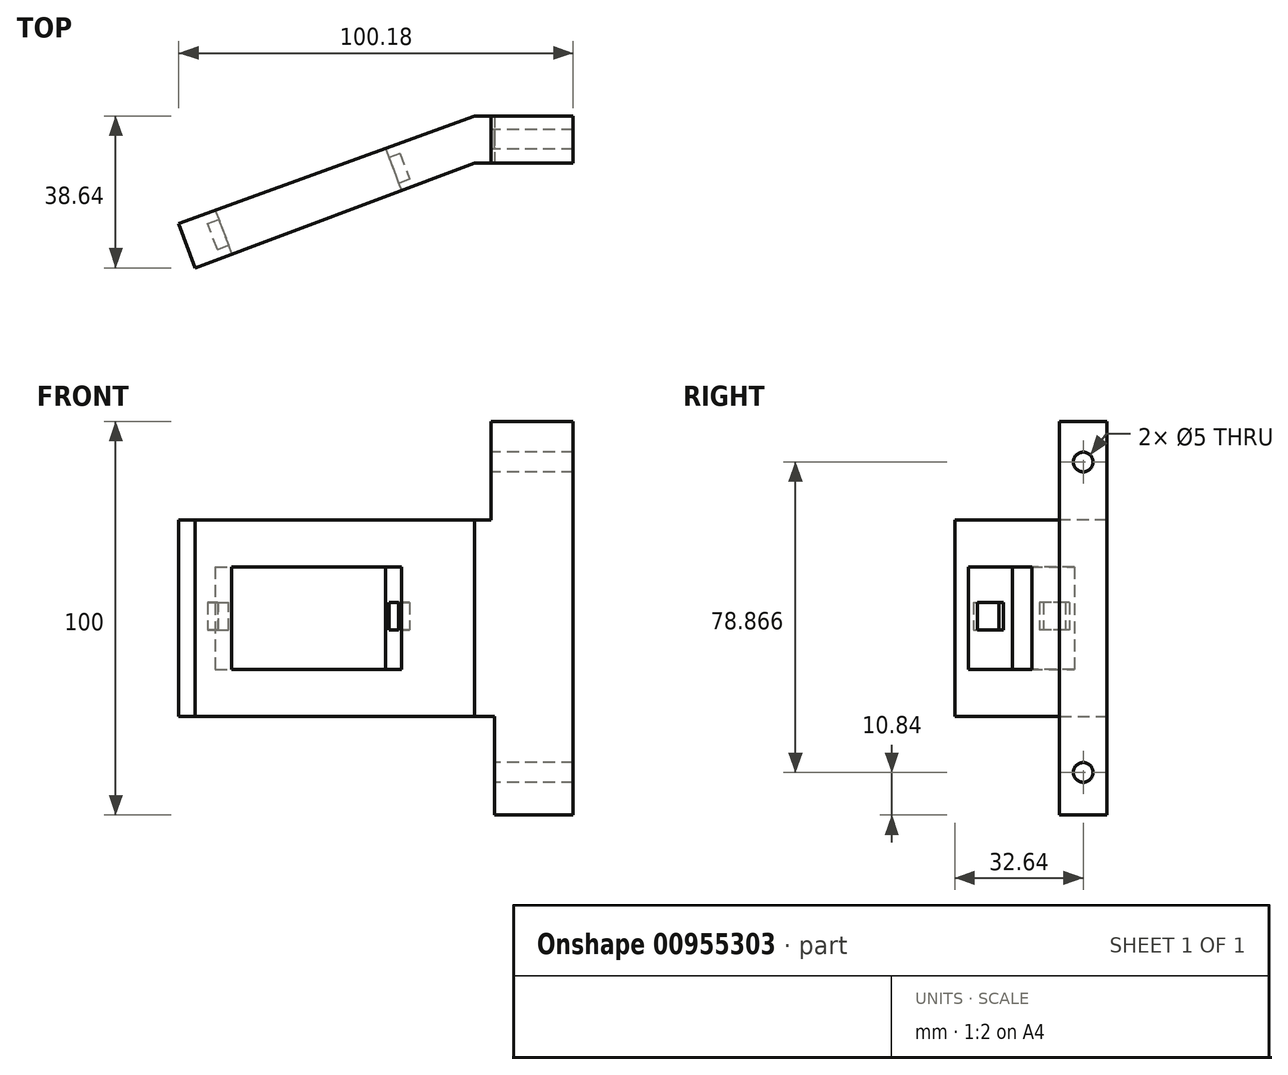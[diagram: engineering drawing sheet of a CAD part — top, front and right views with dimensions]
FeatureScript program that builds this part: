
annotation { "Feature Type Name" : "Feature", "Feature Type Description" : "" }
export const myFeature = defineFeature(function(context is Context, id is Id, definition is map)
    precondition{}
    {
        {
            var Q0;
            Q0=qCreatedBy(makeId("Top.planeOp"),FACE);
            var sketch = newSketch(context, id + "F0", { "sketchPlane" : qUnion([Q0])});
            skLineSegment(sketch, "E0", {"start": v(0, 0) * mm, "end": v(0, 12) * mm});
            skLineSegment(sketch, "E1", {"start": v(0, 12) * mm, "end": v(-25, 12) * mm});
            skLineSegment(sketch, "E2", {"start": v(-25, 12) * mm, "end": v(-100.18, -15.36) * mm});
            skLineSegment(sketch, "E3", {"start": v(-100.18, -15.36) * mm, "end": v(-96.07, -26.64) * mm});
            skLineSegment(sketch, "E4", {"start": v(0, 0) * mm, "end": v(-25, 0) * mm});
            skLineSegment(sketch, "E5", {"start": v(-96.07, -26.64) * mm, "end": v(-25, 0) * mm});
            skSolve(sketch);
        }
        {
            var Q0;
            Q0 = qSketchRegion(id + "F0", true);
            extrude(context, id + "F1", {"entities" : qUnion([Q0]), "depth" : 100 * mm, "offsetDistance" : 25 * mm});
        }
        {
            var Q0;
            Q0=makeQuery(id+"F1.opExtrude","SWEPT_FACE",FACE,{"disambiguationData":[OSD([sQuery(id+"F0.wireOp",EDGE,"E5")])]});
            cPlane(context, id + "F2", {"entities" : qUnion([Q0]), "cplaneType" : CPlaneType.OFFSET, "offset" : 0 * mm, "width" : 150 * mm, "height" : 150 * mm});
        }
        {
            var Q0;
            Q0=qCreatedBy(id+"F2.planeOp",FACE);
            var sketch = newSketch(context, id + "F3", { "sketchPlane" : qUnion([Q0])});
            skLineSegment(sketch, "E6.bottom", {"start": v(-89.3, 63) * mm, "end": v(-43.3, 63) * mm});
            skLineSegment(sketch, "E6.top", {"start": v(-89.3, 37) * mm, "end": v(-43.3, 37) * mm});
            skLineSegment(sketch, "E6.left", {"start": v(-89.3, 63) * mm, "end": v(-89.3, 37) * mm});
            skLineSegment(sketch, "E6.right", {"start": v(-43.3, 63) * mm, "end": v(-43.3, 37) * mm});
            skSolve(sketch);
        }
        {
            var Q0;
            Q0 = qSketchRegion(id + "F3", true);
            extrude(context, id + "F4", {"entities" : qUnion([Q0]), "operationType" : NewBodyOperationType.REMOVE, "oppositeDirection" : true, "depth" : 25 * mm, "offsetDistance" : 25 * mm});
        }
        {
            var Q0;
            Q0=makeQuery(id+"F1.opExtrude","CAP_FACE",FACE,{"disambiguationData":[OSD([sQuery(id+"F0.wireOp",EDGE,"E0"),sQuery(id+"F0.wireOp",EDGE,"E1"),sQuery(id+"F0.wireOp",EDGE,"E2"),sQuery(id+"F0.wireOp",EDGE,"E3"),sQuery(id+"F0.wireOp",EDGE,"E4"),sQuery(id+"F0.wireOp",EDGE,"E5")])],"isStart":false});
            var sketch = newSketch(context, id + "F5", { "sketchPlane" : qUnion([Q0])});
            skLineSegment(sketch, "E7.bottom", {"start": v(-116.92, 30.4) * mm, "end": v(-20, 30.4) * mm});
            skLineSegment(sketch, "E7.top", {"start": v(-116.92, -38.36) * mm, "end": v(-20, -38.36) * mm});
            skLineSegment(sketch, "E7.left", {"start": v(-116.92, 30.4) * mm, "end": v(-116.92, -38.36) * mm});
            skLineSegment(sketch, "E7.right", {"start": v(-20, 30.4) * mm, "end": v(-20, -38.36) * mm});
            skSolve(sketch);
        }
        {
            var Q0;
            {var subQ5=makeQuery(id+"F1.opExtrude","CAP_EDGE",EDGE,{"disambiguationData":[OSD([sQuery(id+"F0.wireOp",EDGE,"E0")])],"isStart":false});Q0=makeQuery(id+"F5.imprint","IMPRINT",FACE,{"disambiguationData":[TD([[makeQuery(id+"F5.imprint","IMPRINT",EDGE,{"derivedFrom":subQ5}),1.0]])]});}
            cPlane(context, id + "F6", {"entities" : qUnion([Q0]), "cplaneType" : CPlaneType.OFFSET, "offset" : 5 * mm, "width" : 150 * mm, "height" : 150 * mm});
        }
        {
            var Q0;
            Q0=qCreatedBy(id+"F6.planeOp",FACE);
            var sketch = newSketch(context, id + "F7", { "sketchPlane" : qUnion([Q0])});
            skLineSegment(sketch, "E8.bottom", {"start": v(-119.42, 33.1) * mm, "end": v(-20.8, 33.1) * mm});
            skLineSegment(sketch, "E8.top", {"start": v(-119.42, -42.01) * mm, "end": v(-20.8, -42.01) * mm});
            skLineSegment(sketch, "E8.left", {"start": v(-119.42, 33.1) * mm, "end": v(-119.42, -42.01) * mm});
            skLineSegment(sketch, "E8.right", {"start": v(-20.8, 33.1) * mm, "end": v(-20.8, -42.01) * mm});
            skSolve(sketch);
        }
        {
            var Q0;
            Q0 = qSketchRegion(id + "F7", true);
            extrude(context, id + "F8", {"entities" : qUnion([Q0]), "operationType" : NewBodyOperationType.REMOVE, "oppositeDirection" : true, "depth" : 30 * mm, "offsetDistance" : 25 * mm});
        }
        {
            var Q0;
            Q0=makeQuery(id+"F1.opExtrude","CAP_FACE",FACE,{"disambiguationData":[OSD([sQuery(id+"F0.wireOp",EDGE,"E0"),sQuery(id+"F0.wireOp",EDGE,"E1"),sQuery(id+"F0.wireOp",EDGE,"E2"),sQuery(id+"F0.wireOp",EDGE,"E3"),sQuery(id+"F0.wireOp",EDGE,"E4"),sQuery(id+"F0.wireOp",EDGE,"E5")])],"isStart":true});
            cPlane(context, id + "F9", {"entities" : qUnion([Q0]), "cplaneType" : CPlaneType.OFFSET, "offset" : 5 * mm, "width" : 150 * mm, "height" : 150 * mm});
        }
        {
            var Q0;
            Q0=qCreatedBy(id+"F9.planeOp",FACE);
            var sketch = newSketch(context, id + "F10", { "sketchPlane" : qUnion([Q0])});
            skLineSegment(sketch, "E9.bottom", {"start": v(-117.91, 40.15) * mm, "end": v(-20, 40.15) * mm});
            skLineSegment(sketch, "E9.top", {"start": v(-117.91, -43.8) * mm, "end": v(-20, -43.8) * mm});
            skLineSegment(sketch, "E9.left", {"start": v(-117.91, 40.15) * mm, "end": v(-117.91, -43.8) * mm});
            skLineSegment(sketch, "E9.right", {"start": v(-20, 40.15) * mm, "end": v(-20, -43.8) * mm});
            skSolve(sketch);
        }
        {
            var Q0;
            Q0 = qSketchRegion(id + "F10", true);
            extrude(context, id + "F11", {"entities" : qUnion([Q0]), "operationType" : NewBodyOperationType.REMOVE, "oppositeDirection" : true, "depth" : 30 * mm, "offsetDistance" : 25 * mm});
        }
        {
            var Q0;
            Q0=makeQuery(id+"F8.boolean.opBoolean","COPY",FACE,{"derivedFrom":makeQuery(id+"F8.opExtrude","SWEPT_FACE",FACE,{"disambiguationData":[OSD([sQuery(id+"F7.wireOp",EDGE,"E8.right")])]})});
            cPlane(context, id + "F12", {"entities" : qUnion([Q0]), "cplaneType" : CPlaneType.OFFSET, "offset" : 5 * mm, "width" : 150 * mm, "height" : 150 * mm});
        }
        {
            var Q0;
            Q0=qCreatedBy(id+"F12.planeOp",FACE);
            var sketch = newSketch(context, id + "F13", { "sketchPlane" : qUnion([Q0])});
            skCircle(sketch, "E10", {"center": v(-6, 89.7) * mm, "radius": 2.5 * mm});
            skSolve(sketch);
        }
        {
            var Q0;
            Q0=makeQuery(id+"F11.boolean.opBoolean","COPY",FACE,{"derivedFrom":makeQuery(id+"F11.opExtrude","SWEPT_FACE",FACE,{"disambiguationData":[OSD([sQuery(id+"F10.wireOp",EDGE,"E9.right")])]})});
            cPlane(context, id + "F14", {"entities" : qUnion([Q0]), "cplaneType" : CPlaneType.OFFSET, "offset" : 5 * mm, "width" : 150 * mm, "height" : 150 * mm});
        }
        {
            var Q0;
            Q0=qCreatedBy(id+"F14.planeOp",FACE);
            var sketch = newSketch(context, id + "F15", { "sketchPlane" : qUnion([Q0])});
            skCircle(sketch, "E11", {"center": v(-6, 10.84) * mm, "radius": 2.5 * mm});
            skSolve(sketch);
        }
        {
            var Q0;
            Q0 = qSketchRegion(id + "F15", true);
            extrude(context, id + "F16", {"entities" : qUnion([Q0]), "operationType" : NewBodyOperationType.REMOVE, "oppositeDirection" : true, "depth" : 30 * mm, "offsetDistance" : 25 * mm});
        }
        {
            var Q0;
            Q0=makeQuery(id+"F13.imprint","IMPRINT",FACE,{"disambiguationData":[TD([[makeQuery(id+"F13.imprint","IMPRINT",EDGE,{"derivedFrom":sQuery(id+"F13.wireOp",EDGE,"E10")}),1.0]])]});
            var Q1;
            Q1=sQuery(id+"F13.wireOp",EDGE,"E10");
            extrude(context, id + "F17", {"entities" : qUnion([Q0]), "operationType" : NewBodyOperationType.REMOVE, "surfaceEntities" : qUnion([Q1]), "oppositeDirection" : true, "depth" : 30 * mm, "offsetDistance" : 25 * mm});
        }
        {
            var Q0;
            Q0=makeQuery(id+"F4.boolean.opBoolean","COPY",FACE,{"derivedFrom":makeQuery(id+"F4.opExtrude","SWEPT_FACE",FACE,{"disambiguationData":[OSD([sQuery(id+"F3.wireOp",EDGE,"E6.right")])]})});
            cPlane(context, id + "F18", {"entities" : qUnion([Q0]), "cplaneType" : CPlaneType.OFFSET, "offset" : 5 * mm, "width" : 150 * mm, "height" : 150 * mm});
        }
        {
            var Q0;
            Q0=qCreatedBy(id+"F18.planeOp",FACE);
            var sketch = newSketch(context, id + "F19", { "sketchPlane" : qUnion([Q0])});
            skLineSegment(sketch, "E12.bottom", {"start": v(-17.74, 54) * mm, "end": v(-10.74, 54) * mm});
            skLineSegment(sketch, "E12.top", {"start": v(-17.74, 47) * mm, "end": v(-10.74, 47) * mm});
            skLineSegment(sketch, "E12.left", {"start": v(-17.74, 54) * mm, "end": v(-17.74, 47) * mm});
            skLineSegment(sketch, "E12.right", {"start": v(-10.74, 54) * mm, "end": v(-10.74, 47) * mm});
            skSolve(sketch);
        }
        {
            var Q0;
            Q0=makeQuery(id+"F19.imprint","IMPRINT",FACE,{"disambiguationData":[TD([[makeQuery(id+"F19.imprint","IMPRINT",EDGE,{"derivedFrom":sQuery(id+"F19.wireOp",EDGE,"E12.bottom")}),-1.0]])]});
            extrude(context, id + "F20", {"entities" : qUnion([Q0]), "operationType" : NewBodyOperationType.REMOVE, "oppositeDirection" : true, "depth" : 8 * mm, "offsetDistance" : 25 * mm});
        }
        {
            var Q0;
            Q0=makeQuery(id+"F4.boolean.opBoolean","COPY",FACE,{"derivedFrom":makeQuery(id+"F4.opExtrude","SWEPT_FACE",FACE,{"disambiguationData":[OSD([sQuery(id+"F3.wireOp",EDGE,"E6.left")])]})});
            cPlane(context, id + "F21", {"entities" : qUnion([Q0]), "cplaneType" : CPlaneType.OFFSET, "offset" : 5 * mm, "width" : 150 * mm, "height" : 150 * mm});
        }
        {
            var Q0;
            Q0=qCreatedBy(id+"F21.planeOp",FACE);
            var sketch = newSketch(context, id + "F22", { "sketchPlane" : qUnion([Q0])});
            skLineSegment(sketch, "E13.bottom", {"start": v(11.18, 54) * mm, "end": v(18.18, 54) * mm});
            skLineSegment(sketch, "E13.top", {"start": v(11.18, 47) * mm, "end": v(18.18, 47) * mm});
            skLineSegment(sketch, "E13.left", {"start": v(11.18, 54) * mm, "end": v(11.18, 47) * mm});
            skLineSegment(sketch, "E13.right", {"start": v(18.18, 54) * mm, "end": v(18.18, 47) * mm});
            skSolve(sketch);
        }
        {
            var Q0;
            Q0 = qSketchRegion(id + "F22", true);
            extrude(context, id + "F23", {"entities" : qUnion([Q0]), "operationType" : NewBodyOperationType.REMOVE, "oppositeDirection" : true, "depth" : 8 * mm, "offsetDistance" : 25 * mm});
        }
    });
